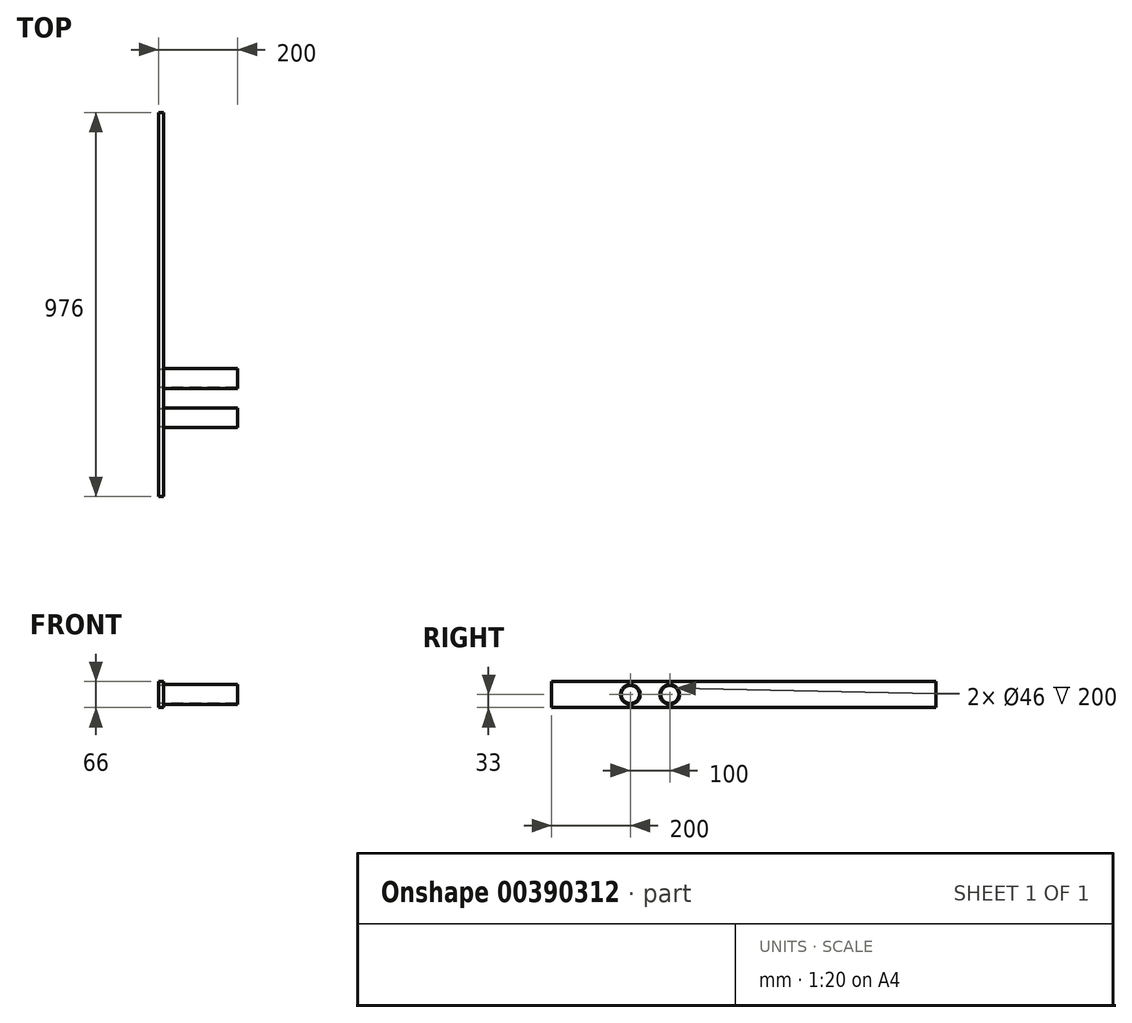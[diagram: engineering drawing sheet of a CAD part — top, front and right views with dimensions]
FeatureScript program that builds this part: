
annotation { "Feature Type Name" : "Feature", "Feature Type Description" : "" }
export const myFeature = defineFeature(function(context is Context, id is Id, definition is map)
    precondition{}
    {
        {
            var Q0;
            Q0=qCreatedBy(makeId("Right.planeOp"),FACE);
            var sketch = newSketch(context, id + "F0", { "sketchPlane" : qUnion([Q0])});
            skLineSegment(sketch, "E0.bottom", {"start": v(0, 0) * mm, "end": v(976, 0) * mm});
            skLineSegment(sketch, "E0.top", {"start": v(0, 66) * mm, "end": v(976, 66) * mm});
            skLineSegment(sketch, "E0.left", {"start": v(0, 0) * mm, "end": v(0, 66) * mm});
            skLineSegment(sketch, "E0.right", {"start": v(976, 0) * mm, "end": v(976, 66) * mm});
            skCircle(sketch, "E1", {"center": v(200, 33) * mm, "radius": 25 * mm});
            skCircle(sketch, "E2", {"center": v(300, 33) * mm, "radius": 25 * mm});
            skCircle(sketch, "E3.0", {"center": v(200, 33) * mm, "radius": 23 * mm});
            skCircle(sketch, "E4.0", {"center": v(300, 33) * mm, "radius": 23 * mm});
            skSolve(sketch);
        }
        {
            var Q0;
            Q0=makeQuery(id+"F0.imprint","IMPRINT",FACE,{"disambiguationData":[TD([[makeQuery(id+"F0.imprint","IMPRINT",EDGE,{"derivedFrom":sQuery(id+"F0.wireOp",EDGE,"E0.bottom")}),1.0]])]});
            extrude(context, id + "F1", {"entities" : qUnion([Q0]), "depth" : 12 * mm});
        }
        {
            var Q0;
            Q0=makeQuery(id+"F0.imprint","IMPRINT",FACE,{"disambiguationData":[TD([[makeQuery(id+"F0.imprint","IMPRINT",EDGE,{"derivedFrom":sQuery(id+"F0.wireOp",EDGE,"E1")}),1.0]])]});
            extrude(context, id + "F2", {"entities" : qUnion([Q0]), "operationType" : NewBodyOperationType.ADD, "depth" : 200 * mm});
        }
        {
            var Q0;
            Q0=makeQuery(id+"F0.imprint","IMPRINT",FACE,{"disambiguationData":[TD([[makeQuery(id+"F0.imprint","IMPRINT",EDGE,{"derivedFrom":sQuery(id+"F0.wireOp",EDGE,"E2")}),1.0]])]});
            extrude(context, id + "F3", {"entities" : qUnion([Q0]), "operationType" : NewBodyOperationType.ADD, "depth" : 200 * mm});
        }
    });
